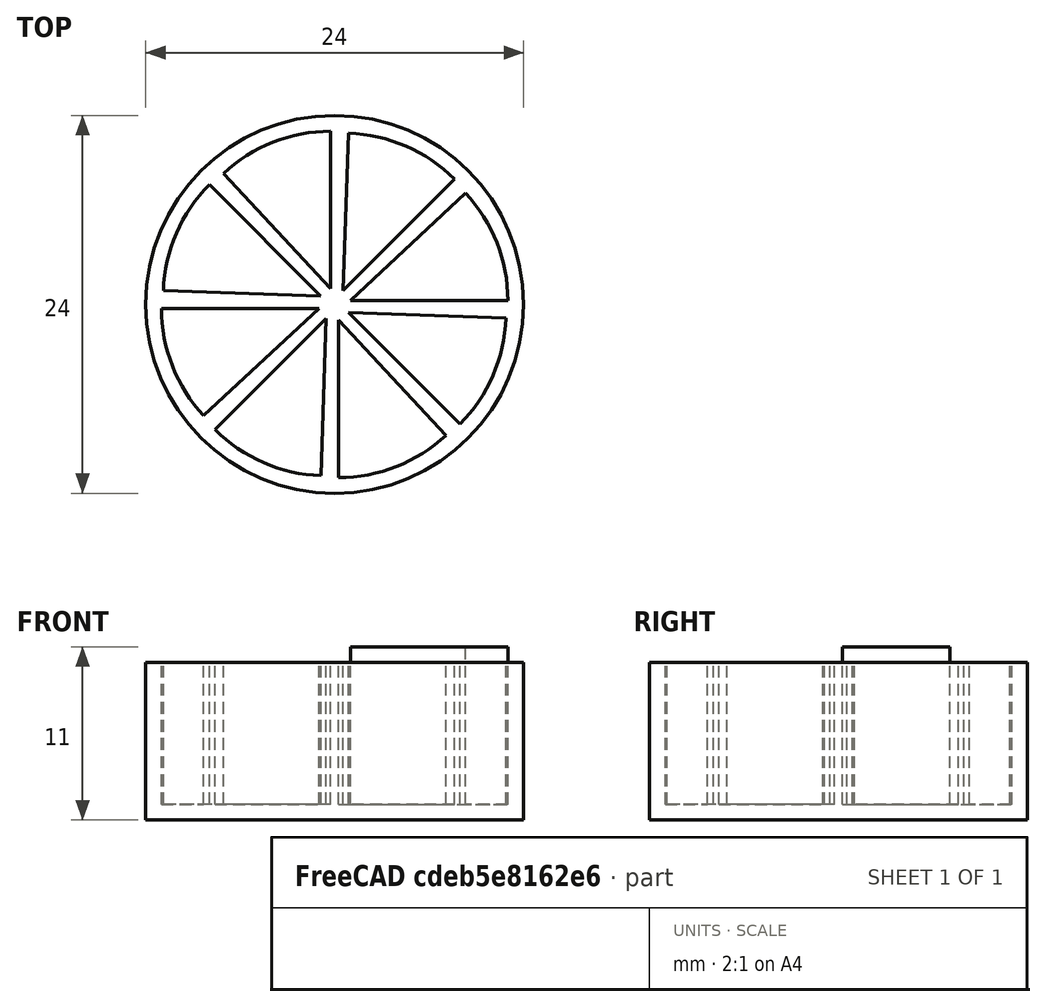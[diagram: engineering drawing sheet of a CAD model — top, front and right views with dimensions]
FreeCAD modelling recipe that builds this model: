
FCSTD DOCUMENT  (FreeCAD 0.21R33771 (Git))
Label: OJT1_T11R02_trivial
License: All rights reserved
LicenseURL: http://en.wikipedia.org/wiki/All_rights_reserved
objects: Part::Cylinder×3, Part::FeaturePython×1, Part::Cut×1
note: 4 computed .brp shape members not serialized (recipe doc carries the construction recipe); baked Part::Feature solids carry a one-line shape summary decoded from their .brp

FEATURE [Part::Cylinder] Cylinder  label="cilindre_caixa"
  Angle = 360
  AttacherType = Attacher::AttachEngine3D
  FirstAngle = 0
  Height = 10
  Radius = 12
  SecondAngle = 0
FEATURE [Part::Cylinder] Cylinder001  label="caserio"
  Angle = 43
  AttacherType = Attacher::AttachEngine3D
  FirstAngle = 0
  Height = 10
  Placement = pos=(1,0.25,1) rot=(0,0,1;0rad)
  Radius = 10
  SecondAngle = 0
FEATURE [Part::FeaturePython] Array  # Draft array (typed FeaturePython)
  AlwaysSyncPlacement = false
  Angle = 360
  ArrayType = 1
  Axis = (0,0,1)
  Base = -> Cylinder001
  Center = (0,0,1)
  Count = 8
  ExpandArray = false
  Fuse = false
  IntervalAxis = (0,0,0)
  IntervalX = (50,0,0)
  IntervalY = (0,50,0)
  IntervalZ = (0,0,50)
  NumberCircles = 3
  NumberPolar = 8
  NumberX = 2
  NumberY = 2
  NumberZ = 1
  PlacementList = 8 placements: [(1,0.25,1),(0.53033,0.883883,1),(-0.25,1,1),(-0.883883,0.53033,1),(-1,-0.25,1),(-0.53033,-0.883883,1),(0.25,-1,1),(0.883883,-0.53033,1)]
  RadialDistance = 50
  ScaleList = (8) [(1,1,1),(1,1,1),(1,1,1),(1,1,1),(1,1,1),(1,1,1),(1,1,1),(1,1,1)]
  Symmetry = 1
  TangentialDistance = 25
FEATURE [Part::Cut] Cut  label="caixa"
  Base = -> Cylinder
  Refine = true
  Tool = -> Array
FEATURE [Part::Cylinder] Cylinder002  label="caserio001"
  Angle = 43
  AttacherType = Attacher::AttachEngine3D
  FirstAngle = 0
  Height = 10
  Placement = pos=(1,0.25,1) rot=(0,0,1;0rad)
  Radius = 10
  SecondAngle = 0
